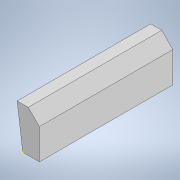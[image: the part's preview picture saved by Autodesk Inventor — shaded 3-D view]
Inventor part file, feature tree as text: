
AUTODESK INVENTOR PART (.ipt)
format: ipt  version: 2021 (Build 250183000, 183)  size: 219,136 bytes
history: native  units: in
note: dims shown in document units (in); Inventor stores cm internally (conversion verified against a paired STEP export)
features: extrude x8, sketch x8, projected_geometry x5
ambient origin geometry x8: Origin, YZ Plane, XZ Plane, XY Plane, X Axis, Y Axis, Z Axis, Center Point
bodies: Solid1 (feature_tree)
feature tree (21):
  extrude  "Extrusion1"  Depth=0.2362in
  extrude  "Extrusion2"  Depth=0.5906in
  extrude  "Extrusion3"  Depth=0.4094in TaperAngle=0.0deg
  extrude  "Extrusion4"  Depth=1.0709in TaperAngle=0.0deg
  extrude  "Extrusion5"  Depth=0.5906in
  extrude  "Extrusion6"  Depth=1.3312in TaperAngle=0.0deg
  extrude  "Extrusion7"  Depth=0.6939in TaperAngle=0.0deg
  extrude  "Extrusion8"  Depth=0.5906in
  sketch  "Sketch14"  dims[d34=0.6939in d35=0.0in d38=0.5906in d39=0.0787in d45=0.0157in d46=0.0157in d47=0.0157in d48=0.0157in d49=0.0787in]
  sketch  "Sketch1"  dims[d0=0.2362in d1=0.4331in]
  sketch  "Sketch2"  dims[d2=0.5906in d4=0.0787in]
  sketch  "Sketch3"  dims[d5=0.0787in d6=0.4094in d7=0.0in]
  projected_geometry  "Projected Loop1"
  sketch  "Sketch7"  dims[d9=0.1181in d12=1.0709in d13=0.0in]
  sketch  "Sketch8"  dims[d14=0.4094in d15=0.0in d19=0.5906in]
  projected_geometry  "Projected Loop4"
  sketch  "Sketch10"  dims[d21=1.3312in d22=0.0in d23=1.3312in d24=0.0in]
  sketch  "Sketch12"  dims[d25=1.1811in d26=0.0787in d27=0.0in d28=0.0in d31=0.6939in d32=0.0in]
  projected_geometry  "Projected Loop6"
  projected_geometry  "Projected Loop8"
  projected_geometry  "Projected Loop9"
